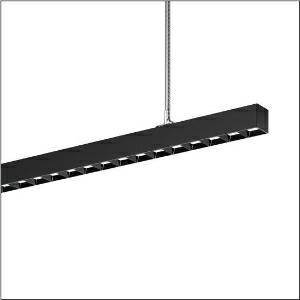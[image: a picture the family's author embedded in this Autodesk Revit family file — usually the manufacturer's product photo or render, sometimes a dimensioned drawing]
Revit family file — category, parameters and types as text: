
# Revit family: silica_r__21_51mx34dc4dbb_b20b
name_source: partatom
category: Lighting Fixtures
units: mm (PartAtom-declared; Revit-internal decimal feet)

## family parameters
Cut with Voids When Loaded = No
Host = Face
Light Source = No
Part Type = Normal
Room Calculation Point = No
Round Connector Dimension = Use Diameter
Shared = No

## types (1)
- --- (1 x LED, 19200 lm, 120.3 W, 4000K)
    Apparent Load = 120 VA
    CIE Flux Codes = 74 94 99 56 100
    Color Rendering = 80
    Color Temperature = 4000K
    Default Elevation = 1800 mm
    Description = Silica® 21, office luminaire, primary light control with darklight reflector, of PMMA, black, light emission: direct/indirect distribution, primary light characteristic: asymmetric, installation type: suspended mounting, LED, rated luminous flux: 19.200lm, luminous efficacy: 160lm/W, light colour: 840, colour temperature: 4000K, control gear: DALI 2, with terminal, 3+2-pole, max. 2.5mm², mains connection: 220..240V, AC, 50/60Hz, rated input power: 120.3W, luminaire housing, of aluminium, matt jet black (RAL 9005), length: 3.004mm, width: 53mm, height: 53mm, protection rating (complete): IP20, insulation class (complete): insulation class I (protective earthing), certification: CE, permissible operating ambient temperature: 0..+35°C, standard: EN 50419, packaging unit: 1 piece
    Height = 53 mm
    Lamp = 1 x LED
    Lamp Light Flux = 19200 lm
    Lamp Power = 120.3 W
    Lamp count = 1
    Length = 3004 mm
    Luminous efficacy = 160 lm/W
    Manufacturer = Siteco
    ModVariant = No
    Model = 51MX34DC4DBB
    Mounting Place = Ceiling
    Mounting Type = Pendant
    Number of Poles = 1
    OnlyDefault = Yes
    Power Factor = 1
    Product Name = Silica® 21
    Product group = office luminaire | ceiling pendant
    ProductGroupID = 904
    Protection Class = Protection class I
    Protection Degree = IP 20
    RLX_Detail_Level = 1
    RLX_Emergency_Light_Flux = 0 lm
    RLX_Emergency_Type = 0
    RLX_Emergency_Type_DB = No
    RlxData = <blob elided: 68069 chars, md5=8c9f3fdd>
    Socket = socket
    Standby Power = 0 W
    System Light Flux = 19200 lm
    System Power = 120 W
    Type Comments = factory setting: luminous flux: 100 % | dim-lin: 254 | 418 mA
    Type Image = l_1335852.jpg
    URL = http://relux.com
    VarID = @adj_120094
    Voltage = 0 V
    Weight = 0.00 kg
    Width = 53 mm

## geometry (parser evidence)
native form markers: Blend x4, Sweep x13
no freeform markers — native parametric forms only
